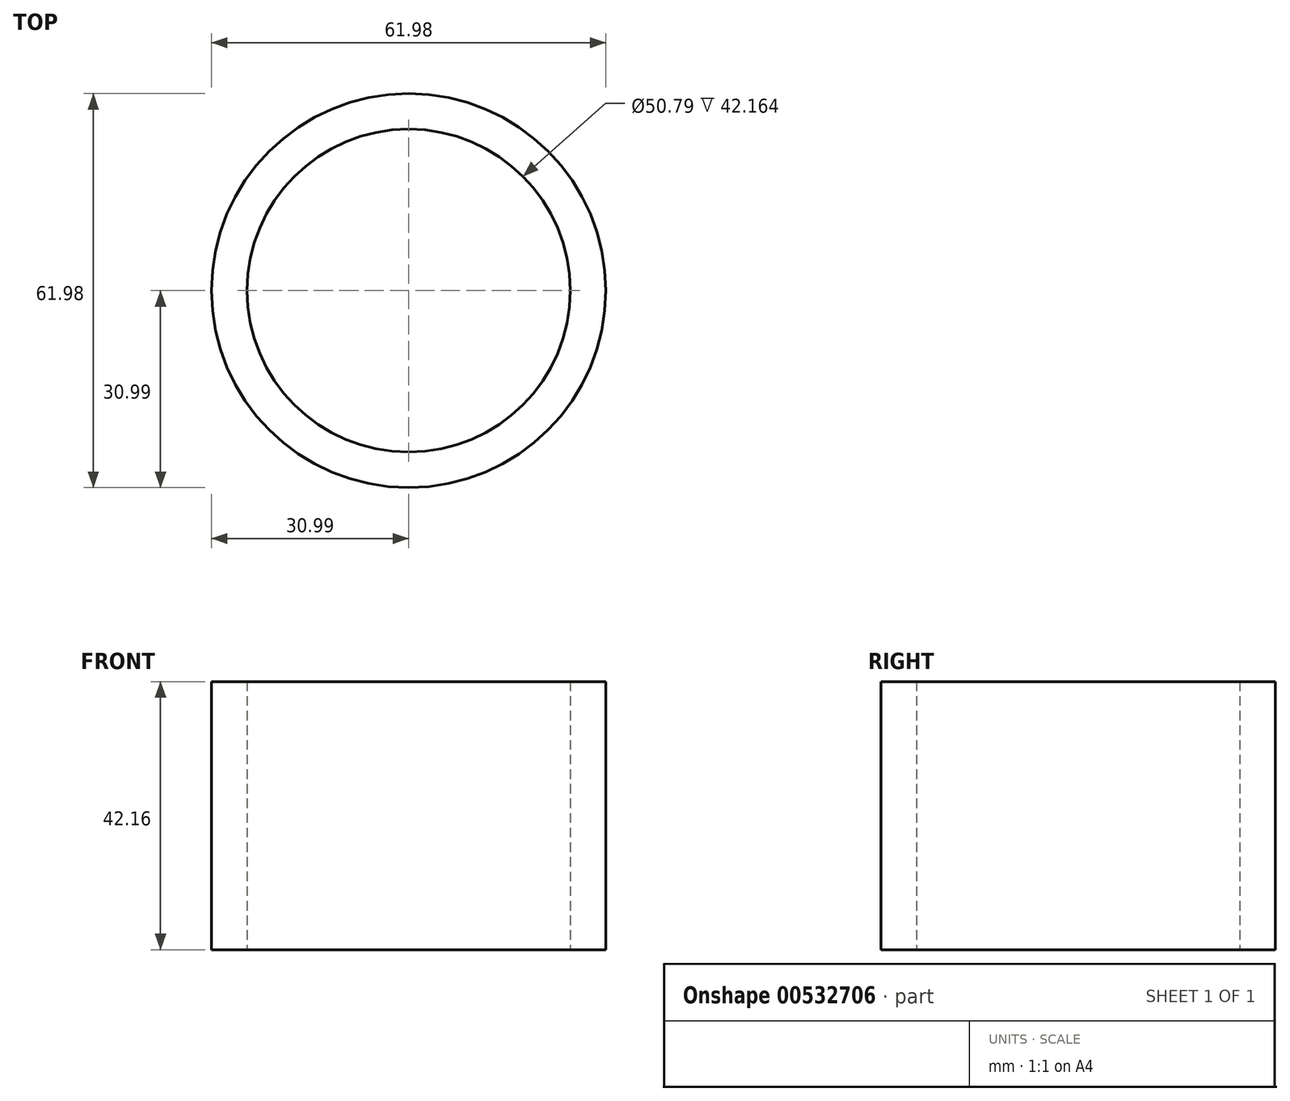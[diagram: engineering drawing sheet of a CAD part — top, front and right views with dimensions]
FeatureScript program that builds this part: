
annotation { "Feature Type Name" : "Feature", "Feature Type Description" : "" }
export const myFeature = defineFeature(function(context is Context, id is Id, definition is map)
    precondition{}
    {
        {
            var Q0;
            Q0=qCreatedBy(makeId("Top.planeOp"),FACE);
            var sketch = newSketch(context, id + "F0", { "sketchPlane" : qUnion([Q0])});
            skLineSegment(sketch, "E0.bottom", {"start": v(-59.92, -56.04) * mm, "end": v(0, -56.04) * mm});
            skLineSegment(sketch, "E0.left", {"start": v(-59.92, -56.04) * mm, "end": v(-59.92, 0) * mm});
            skLineSegment(sketch, "E1.bottom", {"start": v(-59.92, -56.04) * mm, "end": v(0, -56.04) * mm, "construction": true});
            skLineSegment(sketch, "E1.left", {"start": v(-59.92, -56.04) * mm, "end": v(-59.92, 0) * mm, "construction": true});
            skLineSegment(sketch, "E2.MirrorCS", {"start": v(59.92, -56.04) * mm, "end": v(0, -56.04) * mm, "construction": true});
            skLineSegment(sketch, "E3.MirrorCS", {"start": v(59.92, -56.04) * mm, "end": v(59.92, 0) * mm, "construction": true});
            skLineSegment(sketch, "E4.MirrorCS", {"start": v(-59.92, 56.04) * mm, "end": v(-59.92, 0) * mm, "construction": true});
            skLineSegment(sketch, "E5.MirrorCS", {"start": v(-59.92, 56.04) * mm, "end": v(0, 56.04) * mm, "construction": true});
            skLineSegment(sketch, "E6.MirrorCS", {"start": v(59.92, 56.04) * mm, "end": v(0, 56.04) * mm, "construction": true});
            skLineSegment(sketch, "E7.MirrorCS", {"start": v(59.92, 56.04) * mm, "end": v(59.92, 0) * mm, "construction": true});
            skCircle(sketch, "E8", {"center": v(0, 0) * mm, "radius": 30.99 * mm});
            skLineSegment(sketch, "E9", {"start": v(0, -56.04) * mm, "end": v(59.92, -56.04) * mm});
            skCircle(sketch, "E10", {"center": v(0, 0) * mm, "radius": 25.4 * mm});
            skPoint(sketch, "E11.orphan", {"position": v(59.92, 0) * mm});
            skSolve(sketch);
        }
        {
            var Q0;
            Q0 = qSketchRegion(id + "F0", true);
            extrude(context, id + "F1", {"entities" : qUnion([Q0]), "depth" : 42.16 * mm, "offsetDistance" : 25.4 * mm});
        }
    });
